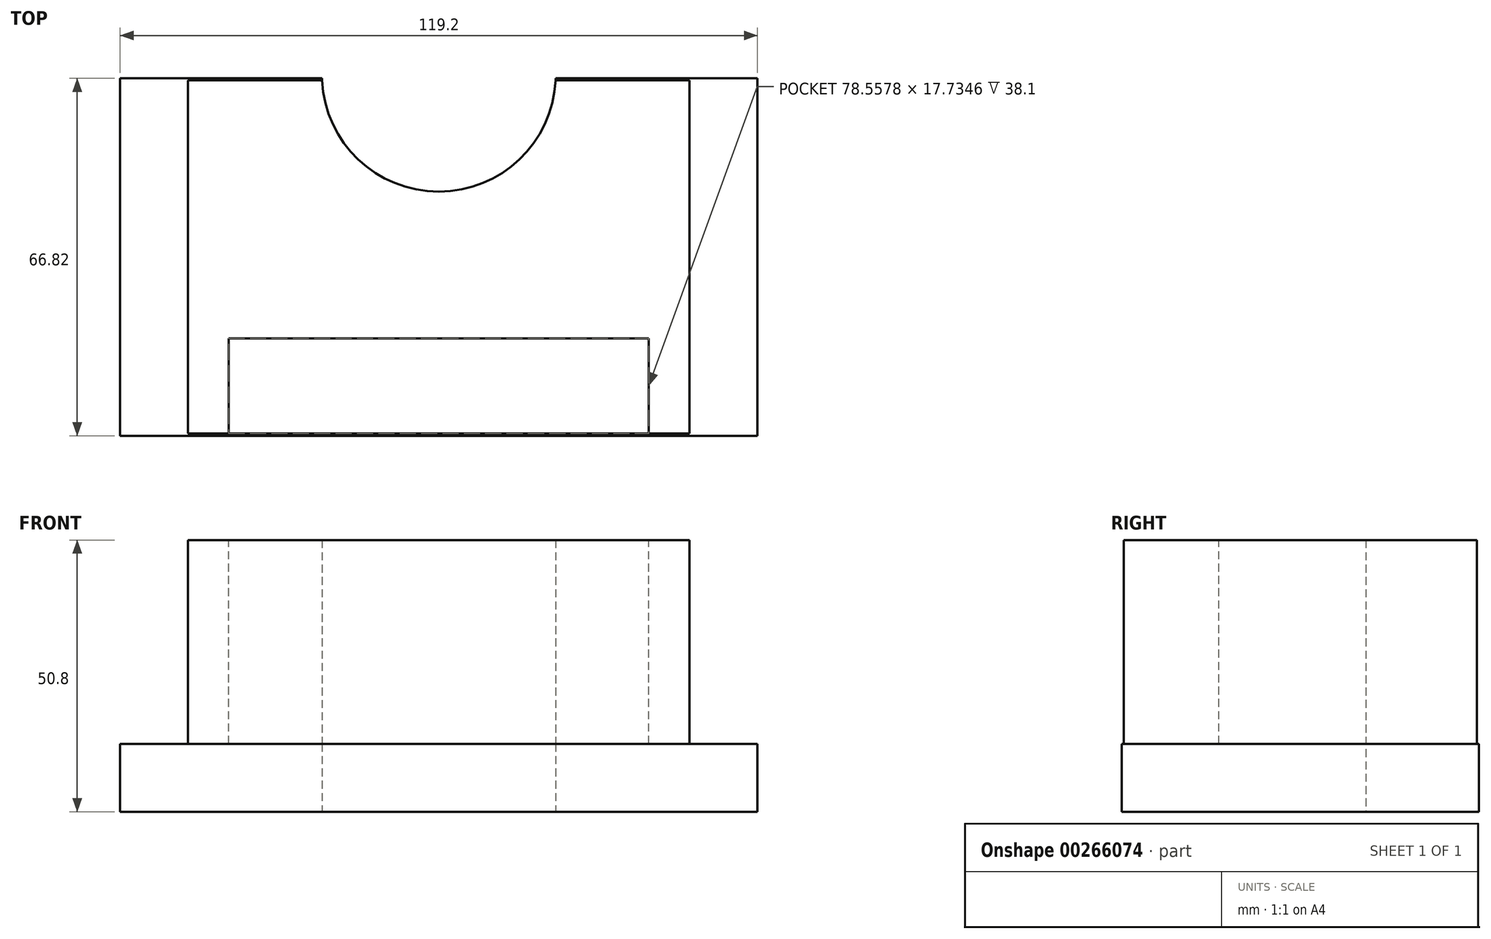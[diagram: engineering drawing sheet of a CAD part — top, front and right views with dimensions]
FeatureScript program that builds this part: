
annotation { "Feature Type Name" : "Feature", "Feature Type Description" : "" }
export const myFeature = defineFeature(function(context is Context, id is Id, definition is map)
    precondition{}
    {
        {
            var Q0;
            Q0=qCreatedBy(makeId("Top.planeOp"),FACE);
            var sketch = newSketch(context, id + "F0", { "sketchPlane" : qUnion([Q0])});
            skLineSegment(sketch, "E0.bottom", {"start": v(59.6, -33.41) * mm, "end": v(-59.6, -33.41) * mm});
            skLineSegment(sketch, "E0.top", {"start": v(59.6, 33.41) * mm, "end": v(-59.6, 33.41) * mm});
            skLineSegment(sketch, "E0.left", {"start": v(59.6, -33.41) * mm, "end": v(59.6, 33.41) * mm});
            skLineSegment(sketch, "E0.right", {"start": v(-59.6, -33.41) * mm, "end": v(-59.6, 33.41) * mm});
            skPoint(sketch, "E0.middle", {"position": v(0, 0) * mm});
            skSolve(sketch);
        }
        {
            var Q0;
            Q0 = qSketchRegion(id + "F0", true);
            extrude(context, id + "F1", {"entities" : qUnion([Q0]), "depth" : 12.7 * mm});
        }
        {
            var Q0;
            Q0=qCreatedBy(makeId("Top.planeOp"),FACE);
            var sketch = newSketch(context, id + "F2", { "sketchPlane" : qUnion([Q0])});
            skLineSegment(sketch, "E1.bottom", {"start": v(-46.9, -33.02) * mm, "end": v(46.9, -33.02) * mm});
            skLineSegment(sketch, "E1.top", {"start": v(-46.9, 33.02) * mm, "end": v(46.9, 33.02) * mm});
            skLineSegment(sketch, "E1.left", {"start": v(-46.9, -33.02) * mm, "end": v(-46.9, 33.02) * mm});
            skLineSegment(sketch, "E1.right", {"start": v(46.9, -33.02) * mm, "end": v(46.9, 33.02) * mm});
            skPoint(sketch, "E1.middle", {"position": v(0, 0) * mm});
            skSolve(sketch);
        }
        {
            var Q0;
            Q0 = qSketchRegion(id + "F2", true);
            extrude(context, id + "F3", {"entities" : qUnion([Q0]), "operationType" : NewBodyOperationType.ADD, "depth" : 50.8 * mm});
        }
        {
            var Q0;
            Q0=qCreatedBy(makeId("Top.planeOp"),FACE);
            var sketch = newSketch(context, id + "F4", { "sketchPlane" : qUnion([Q0])});
            skCircle(sketch, "E2", {"center": v(0, 34.09) * mm, "radius": 21.86 * mm});
            skSolve(sketch);
        }
        {
            var Q0;
            Q0 = qSketchRegion(id + "F4", true);
            extrude(context, id + "F5", {"entities" : qUnion([Q0]), "operationType" : NewBodyOperationType.REMOVE, "depth" : 123.44 * mm});
        }
        {
            var Q0;
            Q0=makeQuery(id+"F3.opExtrude","CAP_FACE",FACE,{"disambiguationData":[OSD([sQuery(id+"F2.wireOp",EDGE,"E1.bottom"),sQuery(id+"F2.wireOp",EDGE,"E1.top"),sQuery(id+"F2.wireOp",EDGE,"E1.left"),sQuery(id+"F2.wireOp",EDGE,"E1.right")])],"isStart":false});
            var sketch = newSketch(context, id + "F6", { "sketchPlane" : qUnion([Q0])});
            skLineSegment(sketch, "E3.bottom", {"start": v(39.28, -15.24) * mm, "end": v(-39.28, -15.24) * mm});
            skLineSegment(sketch, "E3.top", {"start": v(39.28, -32.97) * mm, "end": v(-39.28, -32.97) * mm});
            skLineSegment(sketch, "E3.left", {"start": v(39.28, -15.24) * mm, "end": v(39.28, -32.97) * mm});
            skLineSegment(sketch, "E3.right", {"start": v(-39.28, -15.24) * mm, "end": v(-39.28, -32.97) * mm});
            skPoint(sketch, "E3.middle", {"position": v(0, -24.1) * mm});
            skSolve(sketch);
        }
        {
            var Q0;
            Q0 = qSketchRegion(id + "F6", true);
            extrude(context, id + "F7", {"entities" : qUnion([Q0]), "operationType" : NewBodyOperationType.REMOVE, "oppositeDirection" : true, "depth" : 38.1 * mm});
        }
    });
